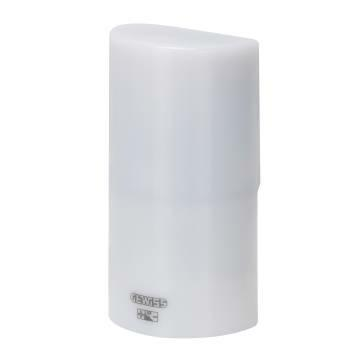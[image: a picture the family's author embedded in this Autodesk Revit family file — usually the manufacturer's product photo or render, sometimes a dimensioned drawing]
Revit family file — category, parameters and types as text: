
# Revit family: Domotics-SerieCivili-GEWISS-27COMBI_SYSTEM-IP65_CREPUSCOLARE
name_source: partatom
category: Modelli generici
revit_build: Autodesk Revit 2016 (Build: 20161004_0715(x64)
units: mm (PartAtom-declared; Revit-internal decimal feet)

## family parameters
Condiviso = No
Host = Superficie
Punto di calcolo locali = No
Può ospitare armatura = No
Quota connettore circolare = Usa diametro
Taglio con vuoti quando caricato = No
Tipo di parte = Normale

## types (1)
- GW27432 - Rivelatore crepuscolare 2-200lux IP65
    Altezza = 106 mm  [stored 0.347769 ft]
    Catalogo = DOMOTICS
    Catalogo Serie = 27COMBI
    Classe isolamento = II
    Codice EAN = 8011564827554
    Codice Electrocod = 0143
    Contatti di uscita = 1NA 16 A (AC1) 250 V ac
    Descrizione = RIVELATORE CREPUSCOLARE 2-200LUX IP65
    Dim. esterne BxHxP (mm) = 55x106x45
    Glow Wire Test = 650°C
    Grado di protezione = IP65
    IDF = 6378bf70-1ce0-4a1f-a238-0e6aa7c17157
    IDT = 09f7fde4-0fd3-4868-bfba-d57139335556
    Immagine tipo = GW27432.jpg
    Larghezza = 55 mm
    Modello = GW27432
    Norma di riferimento = EN 60669-2-1
    Produttore = GEWISS S.p.A.
    Profondità = 45 mm  [stored 0.147638 ft]
    Prospetto di default = 1219 mm
    Regolazione soglia crepuscolare = 0 - 200 lux
    Scheda Tecnica = https://www.gewiss.com
    Temperatura di installazione = -25 +60 °C
    Termopressione con biglia = 70 °C
    URL = https://www.gewiss.com
    Versione file RFA = 18.0

note: [stored X ft] marks values corroborated as IEEE doubles in the binary element streams (Revit-internal decimal feet)

## geometry (parser evidence)
native form markers: Sweep x2
no freeform markers — native parametric forms only
